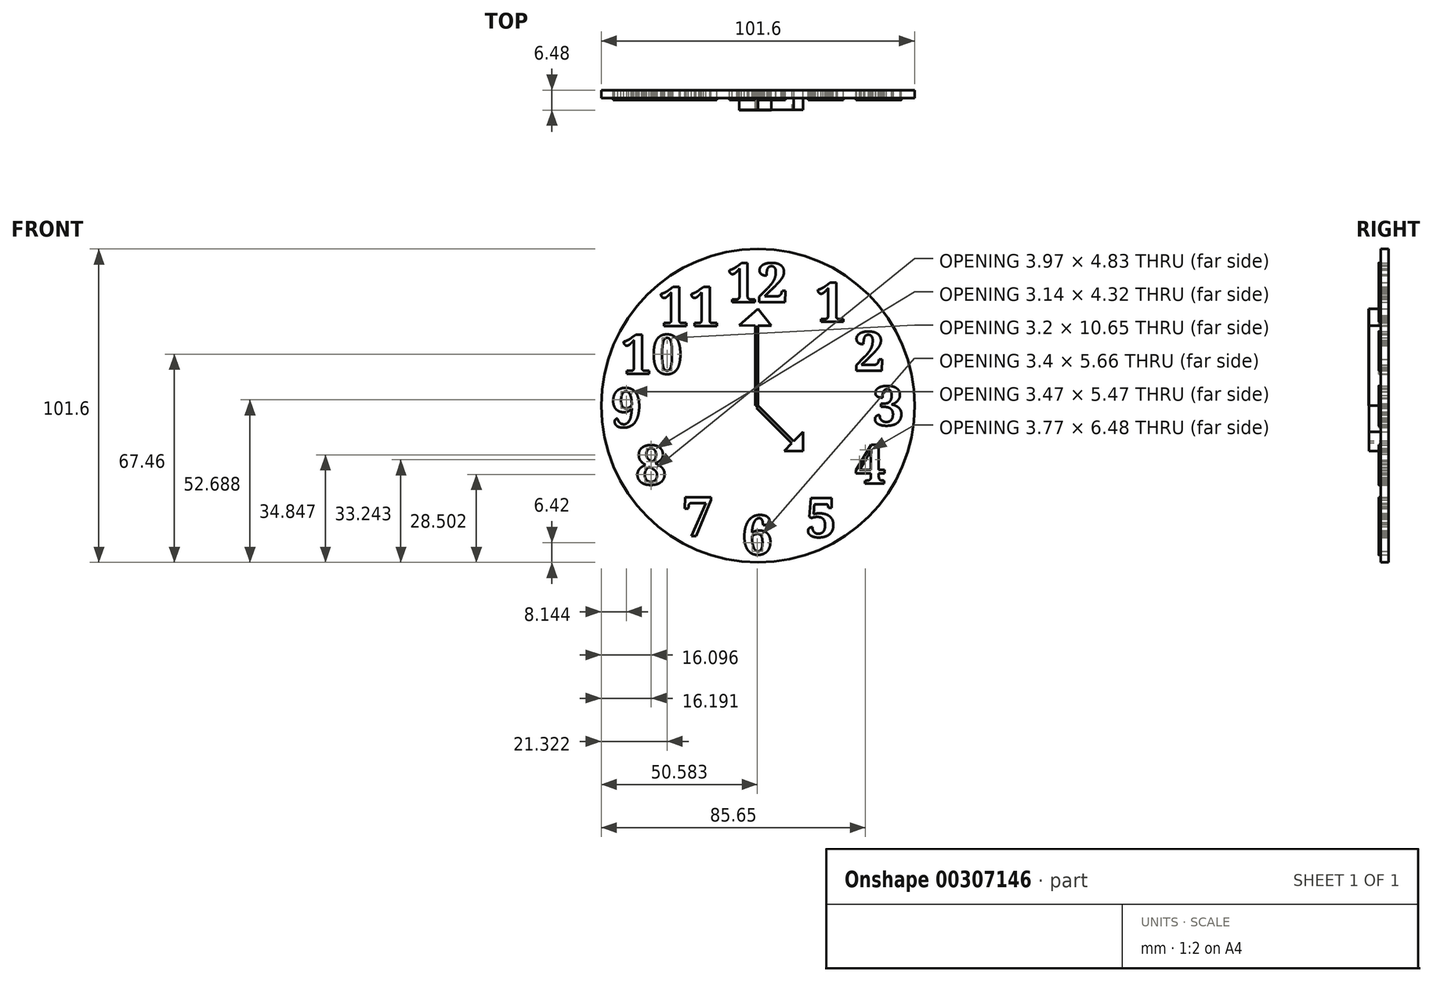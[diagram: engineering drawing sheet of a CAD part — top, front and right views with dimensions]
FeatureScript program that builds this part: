
annotation { "Feature Type Name" : "Feature", "Feature Type Description" : "" }
export const myFeature = defineFeature(function(context is Context, id is Id, definition is map)
    precondition{}
    {
        {
            var Q0;
            Q0=qCreatedBy(makeId("Front.planeOp"),FACE);
            var sketch = newSketch(context, id + "F0", { "sketchPlane" : qUnion([Q0])});
            skCircle(sketch, "E0", {"center": v(0, 0) * mm, "radius": 50.8 * mm});
            skSolve(sketch);
        }
        {
            var Q0;
            Q0=makeQuery(id+"F0.imprint","IMPRINT",FACE,{"disambiguationData":[TD([[makeQuery(id+"F0.imprint","IMPRINT",EDGE,{"derivedFrom":sQuery(id+"F0.wireOp",EDGE,"E0")}),1.0]])]});
            var sketch = newSketch(context, id + "F1", { "sketchPlane" : qUnion([Q0])});
            skText(sketch, "E1", { "text": "12", "fontName": "NotoSerif-Bold.ttf"});
            skText(sketch, "E2", { "text": "6", "fontName": "NotoSerif-Bold.ttf"});
            skText(sketch, "E3", { "text": "9", "fontName": "NotoSerif-Bold.ttf"});
            skText(sketch, "E4", { "text": "3", "fontName": "NotoSerif-Bold.ttf"});
            skText(sketch, "E5", { "text": "7", "fontName": "NotoSerif-Bold.ttf"});
            skText(sketch, "E6", { "text": "8", "fontName": "NotoSerif-Bold.ttf"});
            skText(sketch, "E7", { "text": "10", "fontName": "NotoSerif-Bold.ttf"});
            skText(sketch, "E8", { "text": "11", "fontName": "NotoSerif-Bold.ttf"});
            skText(sketch, "E9", { "text": "1", "fontName": "NotoSerif-Bold.ttf"});
            skPoint(sketch, "E9.firstSnap0", {"position": v(-10.03, 39.88) * mm});
            skText(sketch, "E10", { "text": "2", "fontName": "NotoSerif-Bold.ttf"});
            skText(sketch, "E11", { "text": "4", "fontName": "NotoSerif-Bold.ttf"});
            skText(sketch, "E12", { "text": "5", "fontName": "NotoSerif-Bold.ttf"});
            const initialGuessF1  = {"E1": [-0.01003, 0.03353, 1, 0, 0.0127], "E2": [-0.0052, -0.0482, 1, 0, 0.0127], "E3": [-0.04757, -0.00697, 1, 0, 0.0127], "E4": [0.03745, -0.00635, 1, 0, 0.0127], "E5": [-0.02445, -0.04226, 1, 0, 0.0127], "E6": [-0.0396, -0.02554, 1, 0, 0.0127], "E7": [-0.04427, 0.01036, 1, 0, 0.0127], "E8": [-0.03219, 0.02583, 1, 0, 0.0127], "E9": [0.0187, 0.02718, 1, 0, 0.0127], "E10": [0.03126, 0.01129, 1, 0, 0.0127], "E11": [0.0315, -0.02524, 1, 0, 0.0127], "E12": [0.01554, -0.04257, 1, 0, 0.0127]};
            skSetInitialGuess(sketch, initialGuessF1);
            skSolve(sketch);
        }
        {
            var Q0;
            Q0 = qSketchRegion(id + "F1", true);
            extrude(context, id + "F2", {"entities" : qUnion([Q0]), "depth" : 3.17 * mm});
        }
        {
            var Q0;
            Q0=makeQuery(id+"F0.imprint","IMPRINT",FACE,{"disambiguationData":[TD([[makeQuery(id+"F0.imprint","IMPRINT",EDGE,{"derivedFrom":sQuery(id+"F0.wireOp",EDGE,"E0")}),1.0]])]});
            var sketch = newSketch(context, id + "F3", { "sketchPlane" : qUnion([Q0])});
            skLineSegment(sketch, "E13", {"start": v(0, 0) * mm, "end": v(0, 25.98) * mm});
            skLineSegment(sketch, "E14", {"start": v(0, 0) * mm, "end": v(14.66, -14.66) * mm});
            skLineSegment(sketch, "E15.bottom", {"start": v(14.66, -14.66) * mm, "end": v(8.48, -14.66) * mm});
            skLineSegment(sketch, "E15.top", {"start": v(14.66, -8.48) * mm, "end": v(8.48, -8.48) * mm});
            skLineSegment(sketch, "E15.left", {"start": v(14.66, -14.66) * mm, "end": v(14.66, -8.48) * mm});
            skLineSegment(sketch, "E15.right", {"start": v(8.48, -14.66) * mm, "end": v(8.48, -8.48) * mm});
            skLineSegment(sketch, "E16", {"start": v(14.66, -8.48) * mm, "end": v(8.48, -14.66) * mm});
            skLineSegment(sketch, "E17", {"start": v(0, 0) * mm, "end": v(-0.54, -0.74) * mm});
            skLineSegment(sketch, "E18", {"start": v(-0.54, -0.74) * mm, "end": v(13.38, -14.66) * mm});
            skLineSegment(sketch, "E19", {"start": v(13.38, -14.66) * mm, "end": v(14.66, -14.66) * mm});
            skLineSegment(sketch, "E20", {"start": v(0, 0) * mm, "end": v(-0.9, 0) * mm});
            skLineSegment(sketch, "E21", {"start": v(-0.9, 0) * mm, "end": v(-0.9, 25.88) * mm});
            skLineSegment(sketch, "E22", {"start": v(8.48, -8.48) * mm, "end": v(11.57, -11.57) * mm});
            skLineSegment(sketch, "E23", {"start": v(11.57, -11.57) * mm, "end": v(14.66, -8.48) * mm});
            skLineSegment(sketch, "E24", {"start": v(0, 25.98) * mm, "end": v(4.37, 25.88) * mm});
            skLineSegment(sketch, "E25", {"start": v(-0.9, 25.88) * mm, "end": v(-6.08, 26) * mm});
            skLineSegment(sketch, "E26", {"start": v(-6.08, 26) * mm, "end": v(0, 31.46) * mm});
            skLineSegment(sketch, "E27", {"start": v(0, 31.46) * mm, "end": v(4.37, 25.88) * mm});
            skSolve(sketch);
        }
        {
            var Q0;
            Q0 = qSketchRegion(id + "F3", true);
            extrude(context, id + "F4", {"entities" : qUnion([Q0]), "depth" : 6.35 * mm});
        }
        {
            var Q0;
            Q0=makeQuery(id+"F4.opExtrude","CAP_FACE",FACE,{"disambiguationData":[OSD([sQuery(id+"F3.wireOp",EDGE,"E13"),sQuery(id+"F3.wireOp",EDGE,"E20"),sQuery(id+"F3.wireOp",EDGE,"E21"),sQuery(id+"F3.wireOp",EDGE,"E24"),sQuery(id+"F3.wireOp",EDGE,"E25"),sQuery(id+"F3.wireOp",EDGE,"E26"),sQuery(id+"F3.wireOp",EDGE,"E27")])],"isStart":false});
            var sketch = newSketch(context, id + "F5", { "sketchPlane" : qUnion([Q0])});
            skLineSegment(sketch, "E28", {"start": v(-0.9, 0) * mm, "end": v(0, 0) * mm});
            skSolve(sketch);
        }
        {
            var Q0;
            Q0=makeQuery(id+"F4.opExtrude","CAP_FACE",FACE,{"disambiguationData":[OSD([sQuery(id+"F3.wireOp",EDGE,"E15.bottom"),sQuery(id+"F3.wireOp",EDGE,"E15.top"),sQuery(id+"F3.wireOp",EDGE,"E15.left"),sQuery(id+"F3.wireOp",EDGE,"E15.right"),sQuery(id+"F3.wireOp",EDGE,"E14"),sQuery(id+"F3.wireOp",EDGE,"E17"),sQuery(id+"F3.wireOp",EDGE,"E18"),sQuery(id+"F3.wireOp",EDGE,"E19")])],"isStart":false});
            var sketch = newSketch(context, id + "F6", { "sketchPlane" : qUnion([Q0])});
            skLineSegment(sketch, "E29", {"start": v(8.48, -14.66) * mm, "end": v(14.66, -8.48) * mm});
            skLineSegment(sketch, "E30", {"start": v(14.66, -8.48) * mm, "end": v(8.48, -8.48) * mm});
            skLineSegment(sketch, "E31", {"start": v(8.48, -8.48) * mm, "end": v(11.57, -11.57) * mm});
            skLineSegment(sketch, "E32", {"start": v(8.48, -14.66) * mm, "end": v(8.48, -9.76) * mm});
            skLineSegment(sketch, "E33", {"start": v(8.48, -9.76) * mm, "end": v(10.93, -12.21) * mm});
            skLineSegment(sketch, "E34", {"start": v(10.93, -12.21) * mm, "end": v(8.48, -14.66) * mm});
            skSolve(sketch);
        }
        {
            var Q0;
            Q0=makeQuery(id+"F6.imprint","IMPRINT",FACE,{"disambiguationData":[TD([[makeQuery(id+"F6.imprint","IMPRINT",EDGE,{"derivedFrom":sQuery(id+"F6.wireOp",EDGE,"E32")}),-1.0]])]});
            var Q1;
            {var subQ0=sQuery(id+"F6.wireOp",EDGE,"E30");Q1=makeQuery(id+"F6.imprint","IMPRINT",FACE,{"disambiguationData":[TD([[makeQuery(id+"F6.imprint","IMPRINT",EDGE,{"derivedFrom":subQ0}),1.0]])]});}
            extrude(context, id + "F7", {"entities" : qUnion([Q0, Q1]), "operationType" : NewBodyOperationType.REMOVE, "oppositeDirection" : true, "depth" : 25.4 * mm});
        }
        {
            var Q0;
            Q0=makeQuery(id+"F5.imprint","IMPRINT",FACE,{"disambiguationData":[TD([[makeQuery(id+"F5.imprint","IMPRINT",EDGE,{"derivedFrom":sQuery(id+"F5.wireOp",EDGE,"E28")}),-1.0]])]});
            extrude(context, id + "F8", {"entities" : qUnion([Q0]), "depth" : 0.13 * mm});
        }
        {
            var Q0;
            Q0 = qSketchRegion(id + "F0", true);
            extrude(context, id + "F9", {"entities" : qUnion([Q0]), "depth" : 2.54 * mm});
        }
    });
